# Revit family: Sanitary_Taps-mixers_hansgrohe_74444CHN-Zesis-S-4-hole-rim-mounted-bath-mixer
name_source: partatom
category: Plumbing Fixtures
units: mm (PartAtom-declared; Revit-internal decimal feet)

## family parameters
Always vertical = No
Cut with Voids When Loaded = No
Maintain Annotation Orientation = No
OmniClass Number = 23.31.11.00
OmniClass Title = Faucets
Part Type = Normal
Room Calculation Point = No
Round Connector Dimension = Use Diameter
Shared = No
Work Plane-Based = Yes

## types (2) — shared parameters
Description = Zesis S 4-hole rim mounted bath mixer
Manufacturer = Hansgrohe
Model = 74444CHN
Product Page URL = https://www.hansgrohe.com
Product data url = https://www.bimobject.com
URL = https://www.hansgrohe.com
Version = 1
zero-valued in all types: Default Elevation

## per-type parameters (varying)
| type | Material 1 |
| 007 Chrome | Hansgrohe - Metal - 007 Chrome |
| 677 Matt Black | Hansgrohe - Metal - 677 Matt Black |

## geometry (parser evidence)
native form markers: Sweep x2
no freeform markers — native parametric forms only
